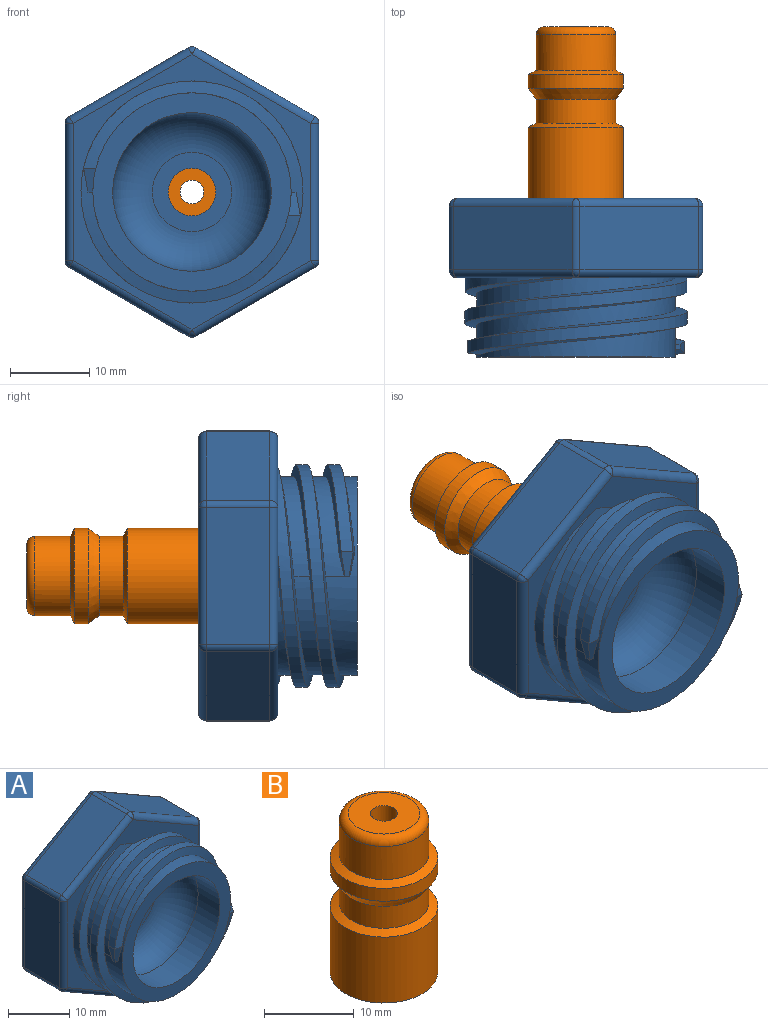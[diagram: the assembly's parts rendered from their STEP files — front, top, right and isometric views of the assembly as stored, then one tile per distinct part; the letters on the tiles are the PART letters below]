
ASSEMBLY  parts=2 mates=1
PART A: 61 faces, bbox 32.1x20.1x36.7 mm
  f0: plane 0.77x0.63mm, normal (0,0,-1), area 0.4mm2, adj f4,f16,f17,f18
  f1: bspline ~28x28mm, area 152.2mm2, adj f3,f4,f6,f16,f17,f19
  f2: bspline ~28x28mm, area 124.7mm2, adj f3,f5,f17,f18,f19
  f3: cylinder r=14mm len=28mm, axis (0,1,0), area 143.4mm2, adj f1,f2,f17,f19
  f4: cylinder r=12.5mm len=25mm, axis (0,1,0), area 238.6mm2, adj f0,f1,f5,f6,f7,f8,f9,f12
  f5: cylinder r=12.5mm len=25mm, axis (0,1,0), area 138.1mm2, adj f2,f4,f8,f18,f19
  f6: cylinder r=12.5mm len=25mm, axis (0,1,0), area 58.9mm2, adj f1,f4,f9,f19
  f7: plane 0.77x0.63mm, normal (0,0,1), area 0.4mm2, adj f4,f13,f14,f15
  f8: bspline ~28x28mm, area 152.2mm2, adj f4,f5,f10,f13,f14,f19
  f9: bspline ~28x28mm, area 124.7mm2, adj f4,f6,f10,f14,f15,f19
  f10: cylinder r=14mm len=28mm, axis (0,1,0), area 143.4mm2, adj f8,f9,f14,f19
  f11: cylinder r=10mm len=20mm, axis (0,1,0), area 314.2mm2, adj f12,f29
  f12: plane 25x25mm, normal (0,-1,0), area 176.7mm2, adj f4,f11
  f13: bspline ~3.02x1.6mm, area 3.3mm2, adj f4,f7,f8,f14
  f14: plane 3.06x1.51mm, normal (0.99,0,0.17), area 3.3mm2, adj f7,f8,f9,f10,f13,f15
  f15: bspline ~2.91x2.17mm, area 3.2mm2, adj f4,f7,f9,f14
  f16: bspline ~3.02x1.6mm, area 3.3mm2, adj f0,f1,f4,f17
  f17: plane 3.06x1.51mm, normal (-0.99,0,-0.17), area 3.3mm2, adj f0,f1,f2,f3,f16,f18
  f18: bspline ~2.91x2.17mm, area 3.2mm2, adj f0,f2,f5,f17
  f19: plane 34.73x30.09mm, normal (0,-1,0), area 234.3mm2, adj f1,f2,f3,f5,f6,f8,f9,f10
  f20: plane 10x10mm, normal (0,-1,0), area 50.3mm2, adj f27,f29
  f21: plane 15x8.66mm, normal (0.5,0,-0.87), area 138.6mm2, adj f45,f54,f55,f59
  f22: plane 17.32x8mm, normal (1,0,0), area 138.6mm2, adj f48,f53,f56,f59
  f23: plane 15x8.66mm, normal (0.5,0,0.87), area 138.6mm2, adj f38,f43,f47,f48
  f24: plane 15x8.66mm, normal (-0.5,0,0.87), area 138.6mm2, adj f30,f33,f37,f38
  f25: plane 17.32x8mm, normal (-1,0,0), area 138.6mm2, adj f30,f34,f35,f36
  f26: plane 15x8.66mm, normal (-0.5,0,-0.87), area 138.6mm2, adj f35,f44,f45,f46
  f27: cylinder r=3mm len=9mm, axis (0,-1,0), area 169.6mm2, adj f20,f60
  f28: plane 34.64x30mm, normal (0,1,0), area 729.2mm2, adj f33,f34,f43,f44,f53,f54,f60
  f29: torus R=5mm, axis (0,-1,0), area 403.8mm2, adj f11,f20
  f30: cylinder r=1mm len=8mm, axis (0,-1,0), area 8.4mm2, adj f24,f25,f31,f32
  f31: sphere r=1mm, area 0.7mm2, adj f30,f33,f34
  f32: sphere r=1mm, area 0.8mm2, adj f30,f36,f37
  f33: cylinder r=1mm len=15.5mm, axis (0.87,0,0.5), area 27.2mm2, adj f24,f28,f31,f39
  f34: cylinder r=1mm len=17.32mm, axis (0,0,1), area 27.2mm2, adj f25,f28,f31,f40
  f35: cylinder r=1mm len=8mm, axis (0,-1,0), area 8.4mm2, adj f25,f26,f40,f41
  f36: cylinder r=1mm len=17.32mm, axis (0,0,-1), area 27.2mm2, adj f19,f25,f32,f41
  f37: cylinder r=1mm len=15.5mm, axis (-0.87,0,-0.5), area 27.2mm2, adj f19,f24,f32,f42
  f38: cylinder r=1mm len=8mm, axis (0,-1,0), area 8.4mm2, adj f23,f24,f39,f42
  f39: sphere r=1mm, area 1mm2, adj f33,f38,f43
  f40: sphere r=1mm, area 0.7mm2, adj f34,f35,f44
  f41: sphere r=1mm, area 0.8mm2, adj f35,f36,f46
  f42: sphere r=1mm, area 1mm2, adj f37,f38,f47
  f43: cylinder r=1mm len=15.5mm, axis (0.87,0,-0.5), area 27.2mm2, adj f23,f28,f39,f49
  f44: cylinder r=1mm len=15.5mm, axis (-0.87,0,0.5), area 27.2mm2, adj f26,f28,f40,f50
  f45: cylinder r=1mm len=8mm, axis (0,-1,0), area 8.4mm2, adj f21,f26,f50,f51
  f46: cylinder r=1mm len=15.5mm, axis (0.87,0,-0.5), area 27.2mm2, adj f19,f26,f41,f51
  f47: cylinder r=1mm len=15.5mm, axis (-0.87,0,0.5), area 27.2mm2, adj f19,f23,f42,f52
  f48: cylinder r=1mm len=8mm, axis (0,-1,0), area 8.4mm2, adj f22,f23,f49,f52
  f49: sphere r=1mm, area 0.8mm2, adj f43,f48,f53
  f50: sphere r=1mm, area 1mm2, adj f44,f45,f54
  f51: sphere r=1mm, area 1mm2, adj f45,f46,f55
  f52: sphere r=1mm, area 1mm2, adj f47,f48,f56
  f53: cylinder r=1mm len=17.32mm, axis (0,0,-1), area 27.2mm2, adj f22,f28,f49,f57
  f54: cylinder r=1mm len=15.5mm, axis (-0.87,0,-0.5), area 27.2mm2, adj f21,f28,f50,f57
  f55: cylinder r=1mm len=15.5mm, axis (0.87,0,0.5), area 27.2mm2, adj f19,f21,f51,f58
  f56: cylinder r=1mm len=17.32mm, axis (0,0,1), area 27.2mm2, adj f19,f22,f52,f58
  f57: sphere r=1mm, area 0.8mm2, adj f53,f54,f59
  f58: sphere r=1mm, area 0.7mm2, adj f55,f56,f59
  f59: cylinder r=1mm len=8mm, axis (0,-1,0), area 8.4mm2, adj f21,f22,f57,f58
  f60: torus R=4mm, axis (0,-1,0), area 33.2mm2, adj f27,f28
PART B: 11 faces, bbox 12x12x21.7 mm
  f0: cone r=6mm half-angle=63.4deg, axis (0,0,-1), area 38.6mm2, adj f1,f8
  f1: cylinder r=6mm len=12mm, axis (0,0,-1), area 339.3mm2, adj f0,f2
  f2: plane 12x12mm, normal (0,0,-1), area 106mm2, adj f1,f9
  f3: plane 8x8mm, normal (0,0,1), area 43.2mm2, adj f9,f10
  f4: cylinder r=5mm len=10mm, axis (0,0,-1), area 141.4mm2, adj f5,f10
  f5: cone r=6mm half-angle=63.4deg, axis (0,0,-1), area 38.6mm2, adj f4,f6
  f6: cylinder r=6mm len=12mm, axis (0,0,-1), area 66mm2, adj f5,f7
  f7: cone r=5mm half-angle=35.5deg, axis (0,0,1), area 59.5mm2, adj f6,f8
  f8: cylinder r=5mm len=10mm, axis (0,0,-1), area 94.2mm2, adj f0,f7
  f9: cylinder r=1.5mm len=21.65mm, axis (0,0,1), area 204mm2, adj f2,f3
  f10: torus R=4mm, axis (0,0,1), area 45.8mm2, adj f3,f4
PLACE A t=(-2.23,-11.59,-2.26)mm
PLACE B rot(axis=(-1,0,0),90deg) t=(-17.48,-1.59,-2.26)mm
MATE fastened B.f0 <-> A.f3  axis (0,1,0) through (-17.48,-1.59,-2.26)mm
